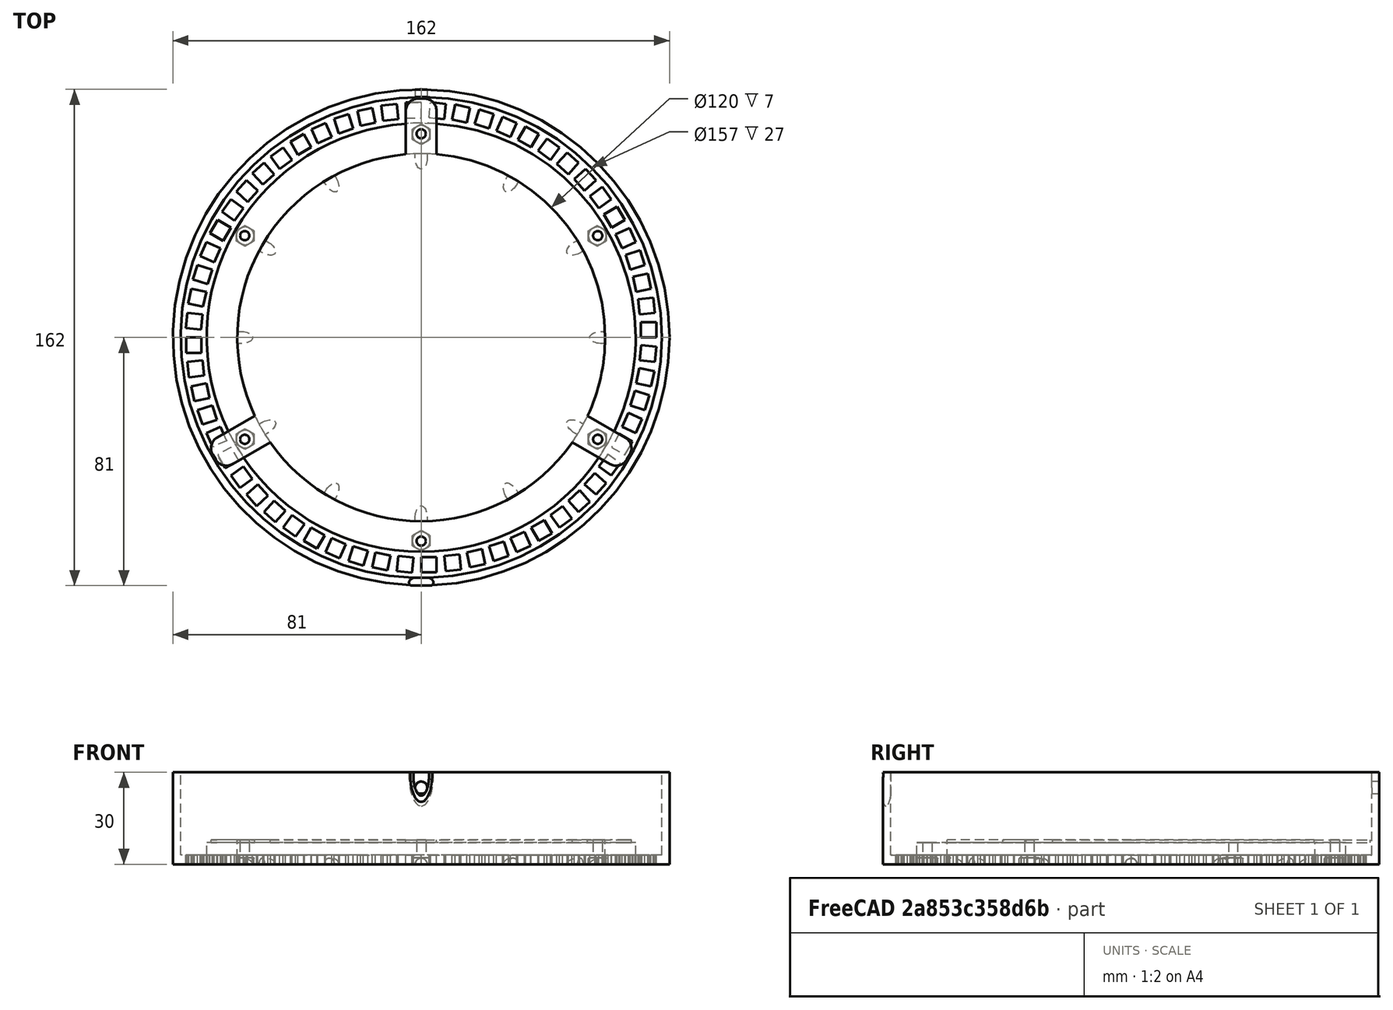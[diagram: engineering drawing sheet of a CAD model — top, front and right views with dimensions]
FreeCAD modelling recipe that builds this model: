
FCSTD DOCUMENT  (FreeCAD 0.16R6707 (Git))
Label: NerfWatchCase
License: CreativeCommons Attribution-ShareAlike
LicenseURL: http://creativecommons.org/licenses/by-sa/4.0/
objects: Part::Cut×10, Part::Cylinder×7, Part::FeaturePython×6, Part::Box×2, Part::MultiFuse×2, Part::Ellipsoid×2, Part::Chamfer×1, PartDesign::Fillet×1
note: 31 computed .brp shape members not serialized (recipe doc carries the construction recipe); baked Part::Feature solids carry a one-line shape summary decoded from their .brp

FEATURE [Part::Cylinder] Cylinder
  Angle = 360
  Height = 30
  Radius = 81
FEATURE [Part::Cylinder] Cylinder001
  Angle = 360
  Height = 50
  Placement = pos=(0,0,7) rot=(0,0,1;0rad)
  Radius = 78.5
FEATURE [Part::Cut] Cut
  Base = -> Cylinder
  Tool = -> Cylinder001
FEATURE [Part::Cylinder] Cylinder002
  Angle = 360
  Height = 30
  Placement = pos=(0,0,-7) rot=(0,0,1;0rad)
  Radius = 60
FEATURE [Part::Cut] Cut001
  Base = -> Cut
  Tool = -> Cylinder002
FEATURE [Part::Box] Box  label="Cube"
  Height = 10
  Length = 5
  Placement = pos=(71.7,0,-2) rot=(0,0,1;0rad)
  Width = 5
FEATURE [Part::FeaturePython] Array  # Draft array (typed FeaturePython)
  Angle = 360
  ArrayType = 1
  Axis = (0,0,10)
  Base = -> Box
  Center = (0,0,0)
  Fuse = false
  IntervalAxis = (0,0,0)
  IntervalX = (1,0,0)
  IntervalY = (0,1,0)
  IntervalZ = (0,0,0)
  NumberPolar = 60
  NumberX = 2
  NumberY = 2
  NumberZ = 1
FEATURE [Part::Cut] Cut002
  Base = -> Cut001
  Tool = -> Array
FEATURE [Part::FeaturePython] Clone  label="Clone of Pocket"  # WARN: FeaturePython — macro-defined, semantics opaque (R4)
  Placement = pos=(0,63,-0.25) rot=(1,0,0;1.5708rad)
  Scale = (1.05,1.05,1.1)
FEATURE [Part::FeaturePython] Array001  # Draft array (typed FeaturePython)
  Angle = 360
  ArrayType = 1
  Axis = (0,0,1)
  Base = -> Clone
  Center = (0,0,0)
  Fuse = false
  IntervalAxis = (0,0,0)
  IntervalX = (1,0,0)
  IntervalY = (0,1,0)
  IntervalZ = (0,0,0)
  NumberPolar = 6
  NumberX = 2
  NumberY = 2
  NumberZ = 1
FEATURE [Part::Cut] Cut003
  Base = -> Cut002
  Tool = -> Array001
FEATURE [Part::Chamfer] Chamfer001
  Edges = 2 edges r=0.1: [Edge6,Edge7]
  Placement = pos=(0,66.5,8) rot=(0,0,0;3.14159rad)
FEATURE [Part::FeaturePython] Array002  # Draft array (typed FeaturePython)
  Angle = 360
  ArrayType = 1
  Axis = (0,0,1)
  Base = -> Chamfer001
  Center = (0,0,0)
  Fuse = false
  IntervalAxis = (0,0,0)
  IntervalX = (1,0,0)
  IntervalY = (0,1,0)
  IntervalZ = (0,0,0)
  NumberPolar = 6
  NumberX = 2
  NumberY = 2
  NumberZ = 1
FEATURE [Part::Cut] Cut004
  Base = -> Cut003
  Tool = -> Array002
FEATURE [Part::Cylinder] Cylinder003
  Angle = 360
  Height = 10
  Radius = 78.5
FEATURE [Part::Cylinder] Cylinder004
  Angle = 360
  Height = 15
  Placement = pos=(0,0,-2) rot=(0,0,1;0rad)
  Radius = 70
FEATURE [Part::Cut] Cut005
  Base = -> Cylinder003
  Placement = pos=(0,0,3) rot=(0,0,1;0rad)
  Tool = -> Cylinder004
FEATURE [Part::Cut] Cut006
  Base = -> Cut004
  Tool = -> Cut005
FEATURE [Part::Cylinder] Cylinder005
  Angle = 360
  Height = 1
  Placement = pos=(0,0,7) rot=(0,0,1;0rad)
  Radius = 60
FEATURE [PartDesign::Fillet] Fillet
  Radius = 4
FEATURE [Part::FeaturePython] Array003  # Draft array (typed FeaturePython)
  Angle = 360
  ArrayType = 1
  Axis = (0,0,1)
  Base = -> Fillet
  Center = (0,0,0)
  Fuse = false
  IntervalAxis = (0,0,0)
  IntervalX = (1,0,0)
  IntervalY = (0,1,0)
  IntervalZ = (0,0,0)
  NumberPolar = 3
  NumberX = 2
  NumberY = 2
  NumberZ = 1
FEATURE [Part::MultiFuse] Fusion  label="Target"
  Shapes = -> [Array003,Cylinder005]
FEATURE [Part::Cylinder] Cylinder006
  Angle = 360
  Height = 100
  Placement = pos=(0,100,25) rot=(1,0,0;1.5708rad)
  Radius = 2
FEATURE [Part::Cut] Cut008
  Base = -> Cut006
  Tool = -> Cylinder006
FEATURE [Part::Ellipsoid] Ellipsoid007
  Angle1 = -90
  Angle2 = 90
  Angle3 = 360
  Placement = pos=(0,-80,29) rot=(0,0,1;0rad)
  Radius1 = 10
  Radius2 = 4
  Radius3 = 2
FEATURE [Part::Cut] Cut009
  Base = -> Cut008
  Tool = -> Ellipsoid007
FEATURE [Part::Ellipsoid] Ellipsoid
  Angle1 = -90
  Angle2 = 90
  Angle3 = 360
  Radius1 = 2
  Radius2 = 2
  Radius3 = 4
FEATURE [Part::Box] Box001  label="Cube001"
  Height = 10
  Length = 10
  Placement = pos=(-5,-5,-10) rot=(0,0,1;0rad)
  Width = 10
FEATURE [Part::Cut] Cut010
  Base = -> Ellipsoid
  Placement = pos=(0,59,0) rot=(0,0,1;0rad)
  Tool = -> Box001
FEATURE [Part::FeaturePython] Array004  label="Horas"  # Draft array (typed FeaturePython)
  Angle = 360
  ArrayType = 1
  Axis = (0,0,1)
  Base = -> Cut010
  Center = (0,0,0)
  Fuse = false
  IntervalAxis = (0,0,0)
  IntervalX = (1,0,0)
  IntervalY = (0,1,0)
  IntervalZ = (0,0,0)
  NumberPolar = 12
  NumberX = 2
  NumberY = 2
  NumberZ = 1
FEATURE [Part::MultiFuse] Fusion001  label="WatchCase"
  Shapes = -> [Cut009,Array004]
